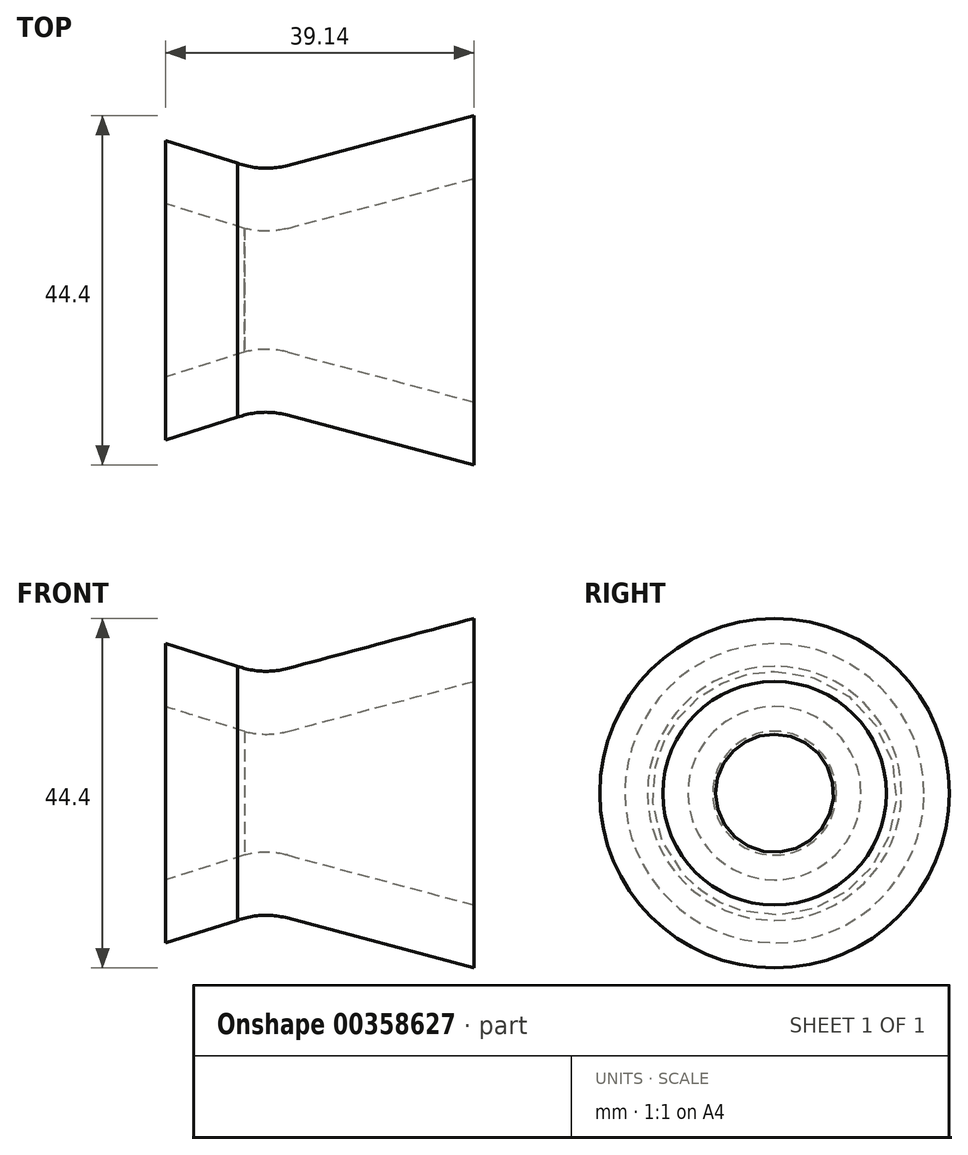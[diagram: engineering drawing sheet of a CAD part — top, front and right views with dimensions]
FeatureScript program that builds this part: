
annotation { "Feature Type Name" : "Feature", "Feature Type Description" : "" }
export const myFeature = defineFeature(function(context is Context, id is Id, definition is map)
    precondition{}
    {
        {
            var Q0;
            Q0=qCreatedBy(makeId("Front.planeOp"),FACE);
            var sketch = newSketch(context, id + "F0", { "sketchPlane" : qUnion([Q0])});
            skLineSegment(sketch, "E0", {"start": v(0, 0) * mm, "end": v(26.4, 0) * mm, "construction": true});
            skLineSegment(sketch, "E1", {"start": v(0, 0) * mm, "end": v(0, 18.1) * mm, "construction": true});
            skLineSegment(sketch, "E2", {"start": v(26.4, 0) * mm, "end": v(26.4, 14.2) * mm, "construction": true});
            skLineSegment(sketch, "E3", {"start": v(26.4, 14.2) * mm, "end": v(2.74, 7.86) * mm});
            skArc(sketch, "E4", {"start": v(-3.6, 8.13) * mm, "mid": v(-0.45, 7.5) * mm, "end": v(2.74, 7.86) * mm});
            skLineSegment(sketch, "E5", {"start": v(2.74, 7.86) * mm, "end": v(-2.74, 7.86) * mm, "construction": true});
            skLineSegment(sketch, "E6", {"start": v(-2.74, 7.86) * mm, "end": v(-12.74, 11) * mm});
            skLineSegment(sketch, "E7", {"start": v(-12.74, 11) * mm, "end": v(-12.74, 19) * mm});
            skLineSegment(sketch, "E8", {"start": v(26.4, 14.2) * mm, "end": v(26.4, 22.2) * mm});
            skLineSegment(sketch, "E9", {"start": v(2.74, 7.86) * mm, "end": v(2.74, 15.86) * mm, "construction": true});
            skLineSegment(sketch, "E10", {"start": v(2.74, 15.86) * mm, "end": v(26.4, 22.2) * mm});
            skArc(sketch, "E11", {"start": v(-3.6, 16.13) * mm, "mid": v(-0.45, 15.5) * mm, "end": v(2.74, 15.86) * mm});
            skLineSegment(sketch, "E12", {"start": v(-2.74, 15.86) * mm, "end": v(-12.74, 19) * mm});
            skSolve(sketch);
        }
        {
            var Q0;
            {var subQ5=sQuery(id+"F0.wireOp",EDGE,"E3");Q0=makeQuery(id+"F0.imprint","IMPRINT",FACE,{"disambiguationData":[TD([[makeQuery(id+"F0.imprint","IMPRINT",EDGE,{"derivedFrom":subQ5}),-1.0]])]});}
            var Q1;
            Q1=sQuery(id+"F0.wireOp",EDGE,"E0");
            revolve(context, id + "F1", {"entities" : qUnion([Q0]), "axis" : qUnion([Q1]), "revolveType" : RevolveType.FULL});
        }
    });
